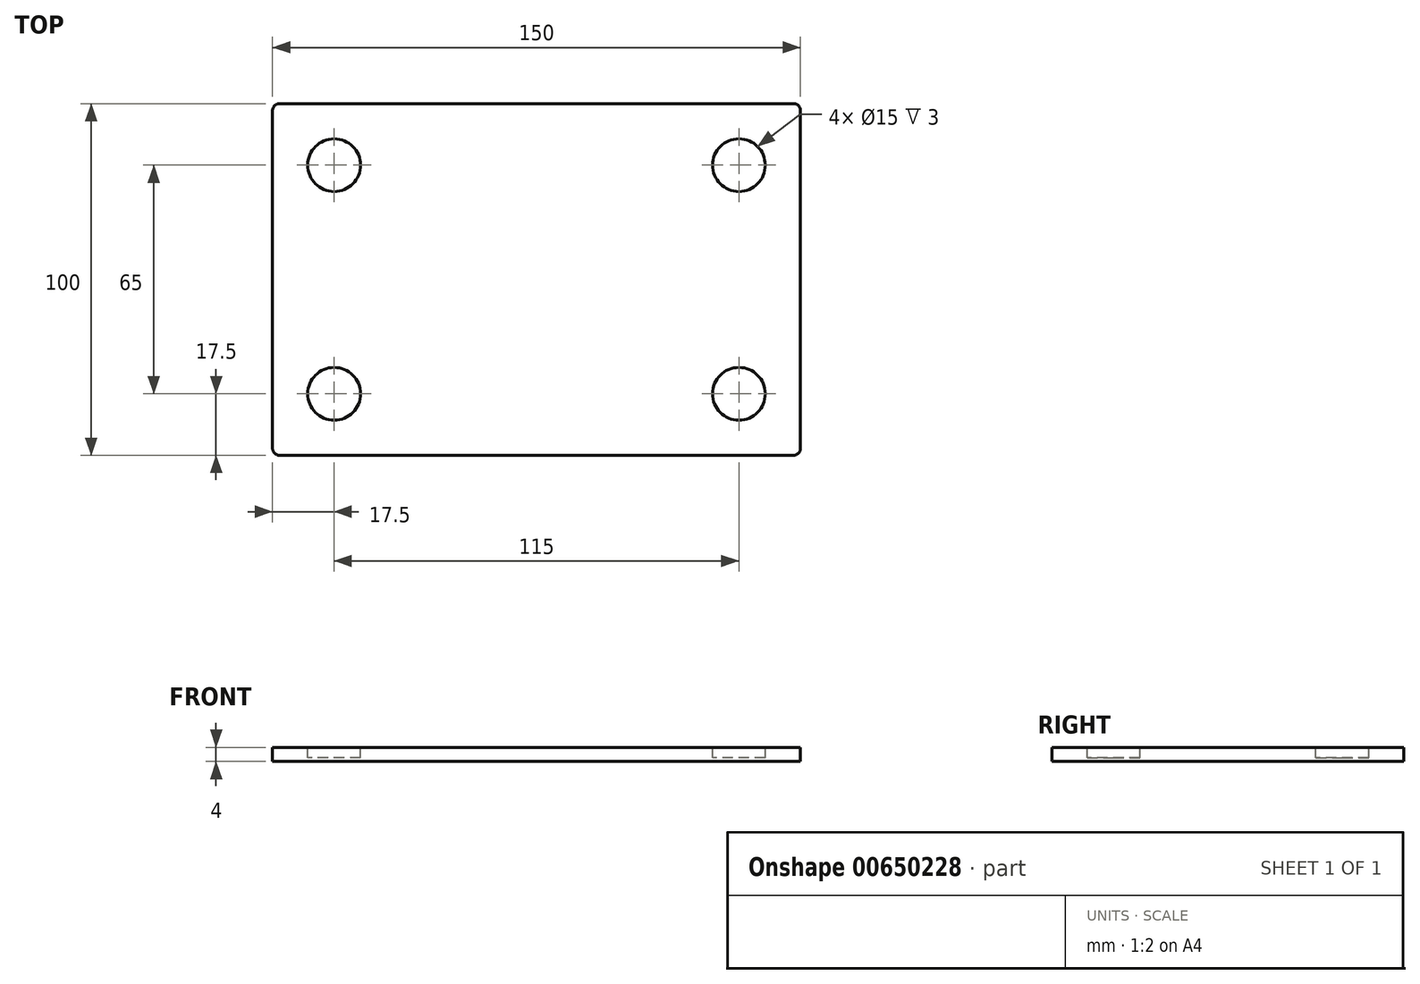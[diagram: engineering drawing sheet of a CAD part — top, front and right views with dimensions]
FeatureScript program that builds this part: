
annotation { "Feature Type Name" : "Feature", "Feature Type Description" : "" }
export const myFeature = defineFeature(function(context is Context, id is Id, definition is map)
    precondition{}
    {
        {
            var Q0;
            Q0=qCreatedBy(makeId("Top.planeOp"),FACE);
            var sketch = newSketch(context, id + "F0", { "sketchPlane" : qUnion([Q0])});
            skLineSegment(sketch, "E0.bottom", {"start": v(0, 0) * mm, "end": v(150, 0) * mm});
            skLineSegment(sketch, "E0.top", {"start": v(0, 100) * mm, "end": v(150, 100) * mm});
            skLineSegment(sketch, "E0.left", {"start": v(0, 0) * mm, "end": v(0, 100) * mm});
            skLineSegment(sketch, "E0.right", {"start": v(150, 0) * mm, "end": v(150, 100) * mm});
            skSolve(sketch);
        }
        {
            var Q0;
            Q0=makeQuery(id+"F0.imprint","IMPRINT",FACE,{"disambiguationData":[TD([[makeQuery(id+"F0.imprint","IMPRINT",EDGE,{"derivedFrom":sQuery(id+"F0.wireOp",EDGE,"E0.bottom")}),1.0]])]});
            extrude(context, id + "F1", {"entities" : qUnion([Q0]), "depth" : 4 * mm, "offsetDistance" : 25 * mm});
        }
        {
            var Q0;
            Q0=makeQuery(id+"F1.opExtrude","CAP_FACE",FACE,{"disambiguationData":[OSD([sQuery(id+"F0.wireOp",EDGE,"E0.bottom"),sQuery(id+"F0.wireOp",EDGE,"E0.top"),sQuery(id+"F0.wireOp",EDGE,"E0.left"),sQuery(id+"F0.wireOp",EDGE,"E0.right")])],"isStart":false});
            var sketch = newSketch(context, id + "F2", { "sketchPlane" : qUnion([Q0])});
            skCircle(sketch, "E1", {"center": v(17.5, 82.5) * mm, "radius": 7.5 * mm});
            skCircle(sketch, "E2", {"center": v(132.5, 82.5) * mm, "radius": 7.5 * mm});
            skCircle(sketch, "E3", {"center": v(17.5, 17.5) * mm, "radius": 7.5 * mm});
            skCircle(sketch, "E4", {"center": v(132.5, 17.5) * mm, "radius": 7.5 * mm});
            skSolve(sketch);
        }
        {
            var Q0;
            Q0=makeQuery(id+"F2.imprint","IMPRINT",FACE,{"disambiguationData":[TD([[makeQuery(id+"F2.imprint","IMPRINT",EDGE,{"derivedFrom":sQuery(id+"F2.wireOp",EDGE,"E1")}),1.0]])]});
            var Q1;
            Q1=makeQuery(id+"F2.imprint","IMPRINT",FACE,{"disambiguationData":[TD([[makeQuery(id+"F2.imprint","IMPRINT",EDGE,{"derivedFrom":sQuery(id+"F2.wireOp",EDGE,"E2")}),1.0]])]});
            var Q2;
            Q2=makeQuery(id+"F2.imprint","IMPRINT",FACE,{"disambiguationData":[TD([[makeQuery(id+"F2.imprint","IMPRINT",EDGE,{"derivedFrom":sQuery(id+"F2.wireOp",EDGE,"E4")}),1.0]])]});
            var Q3;
            Q3=makeQuery(id+"F2.imprint","IMPRINT",FACE,{"disambiguationData":[TD([[makeQuery(id+"F2.imprint","IMPRINT",EDGE,{"derivedFrom":sQuery(id+"F2.wireOp",EDGE,"E3")}),1.0]])]});
            extrude(context, id + "F3", {"entities" : qUnion([Q0, Q1, Q2, Q3]), "operationType" : NewBodyOperationType.REMOVE, "oppositeDirection" : true, "depth" : 3 * mm, "offsetDistance" : 25 * mm});
        }
        {
            var Q0;
            Q0=makeQuery(id+"F1.opExtrude","SWEPT_EDGE",EDGE,{"disambiguationData":[OSD([sQuery(id+"F0.wireOp",EDGE,"E0.bottom"),sQuery(id+"F0.wireOp",EDGE,"E0.left")])]});
            var Q1;
            Q1=makeQuery(id+"F1.opExtrude","SWEPT_EDGE",EDGE,{"disambiguationData":[OSD([sQuery(id+"F0.wireOp",EDGE,"E0.top"),sQuery(id+"F0.wireOp",EDGE,"E0.left")])]});
            var Q2;
            Q2=makeQuery(id+"F1.opExtrude","SWEPT_EDGE",EDGE,{"disambiguationData":[OSD([sQuery(id+"F0.wireOp",EDGE,"E0.top"),sQuery(id+"F0.wireOp",EDGE,"E0.right")])]});
            var Q3;
            Q3=makeQuery(id+"F1.opExtrude","SWEPT_EDGE",EDGE,{"disambiguationData":[OSD([sQuery(id+"F0.wireOp",EDGE,"E0.bottom"),sQuery(id+"F0.wireOp",EDGE,"E0.right")])]});
            fillet(context, id + "F4", {"entities" : qUnion([Q0, Q1, Q2, Q3]), "radius" : 2 * mm, "tangentPropagation" : true, "allowEdgeOverflow" : false});
        }
    });
